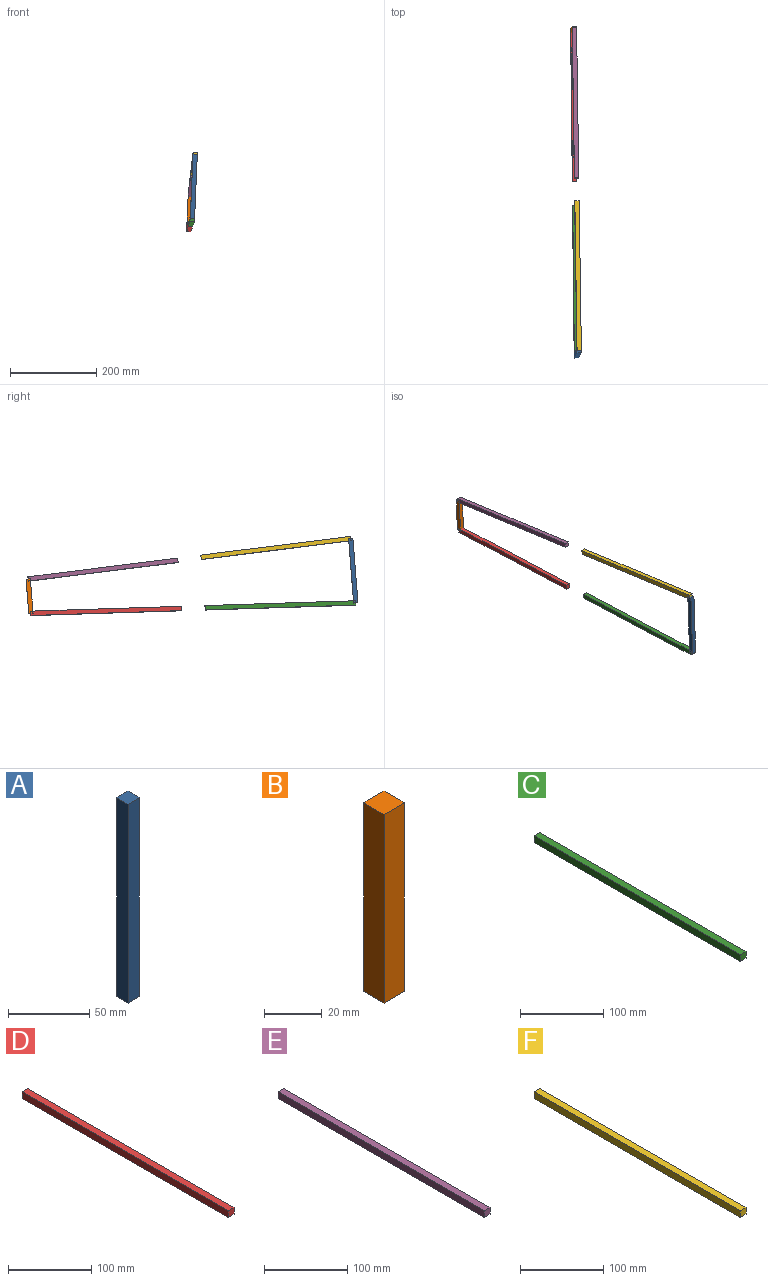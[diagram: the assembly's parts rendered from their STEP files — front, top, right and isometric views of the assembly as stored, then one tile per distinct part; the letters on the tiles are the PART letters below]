
ASSEMBLY  parts=6 mates=8
PART A: 6 faces, bbox 10x10x150 mm
  f0: plane 10x10mm, normal (0,0,1), area 100mm2, adj f1,f3,f4,f5
  f1: plane 150x10mm, normal (0,-1,0), area 1500mm2, adj f0,f2,f4,f5
  f2: plane 10x10mm, normal (0,0,-1), area 100mm2, adj f1,f3,f4,f5
  f3: plane 150x10mm, normal (0,1,0), area 1500mm2, adj f0,f2,f4,f5
  f4: plane 150x10mm, normal (1,0,0), area 1500mm2, adj f0,f1,f2,f3
  f5: plane 150x10mm, normal (-1,0,0), area 1500mm2, adj f0,f1,f2,f3
PART B: 6 faces, bbox 10x10x80 mm
  f0: plane 10x10mm, normal (0,0,1), area 100mm2, adj f1,f3,f4,f5
  f1: plane 80x10mm, normal (0,-1,0), area 800mm2, adj f0,f2,f4,f5
  f2: plane 10x10mm, normal (0,0,-1), area 100mm2, adj f1,f3,f4,f5
  f3: plane 80x10mm, normal (0,1,0), area 800mm2, adj f0,f2,f4,f5
  f4: plane 80x10mm, normal (1,0,0), area 800mm2, adj f0,f1,f2,f3
  f5: plane 80x10mm, normal (-1,0,0), area 800mm2, adj f0,f1,f2,f3
PART C: 6 faces, bbox 10x350x10 mm
  f0: plane 350x10mm, normal (0,0,1), area 3500mm2, adj f1,f3,f4,f5
  f1: plane 10x10mm, normal (0,-1,0), area 100mm2, adj f0,f2,f4,f5
  f2: plane 350x10mm, normal (0,0,-1), area 3500mm2, adj f1,f3,f4,f5
  f3: plane 10x10mm, normal (0,1,0), area 100mm2, adj f0,f2,f4,f5
  f4: plane 350x10mm, normal (1,0,0), area 3500mm2, adj f0,f1,f2,f3
  f5: plane 350x10mm, normal (-1,0,0), area 3500mm2, adj f0,f1,f2,f3
PART D: 6 faces, bbox 10x350x10 mm
  f0: plane 10x10mm, normal (0,1,0), area 100mm2, adj f1,f3,f4,f5
  f1: plane 350x10mm, normal (0,0,1), area 3500mm2, adj f0,f2,f4,f5
  f2: plane 10x10mm, normal (0,-1,0), area 100mm2, adj f1,f3,f4,f5
  f3: plane 350x10mm, normal (0,0,-1), area 3500mm2, adj f0,f2,f4,f5
  f4: plane 350x10mm, normal (1,0,0), area 3500mm2, adj f0,f1,f2,f3
  f5: plane 350x10mm, normal (-1,0,0), area 3500mm2, adj f0,f1,f2,f3
PART E: 6 faces, bbox 10x350x10 mm
  f0: plane 350x10mm, normal (0,0,-1), area 3500mm2, adj f1,f3,f4,f5
  f1: plane 10x10mm, normal (0,1,0), area 100mm2, adj f0,f2,f4,f5
  f2: plane 350x10mm, normal (0,0,1), area 3500mm2, adj f1,f3,f4,f5
  f3: plane 10x10mm, normal (0,-1,0), area 100mm2, adj f0,f2,f4,f5
  f4: plane 350x10mm, normal (1,0,0), area 3500mm2, adj f0,f1,f2,f3
  f5: plane 350x10mm, normal (-1,0,0), area 3500mm2, adj f0,f1,f2,f3
PART F: 6 faces, bbox 10x350x10 mm
  f0: plane 10x10mm, normal (0,-1,0), area 100mm2, adj f1,f3,f4,f5
  f1: plane 350x10mm, normal (0,0,-1), area 3500mm2, adj f0,f2,f4,f5
  f2: plane 10x10mm, normal (0,1,0), area 100mm2, adj f1,f3,f4,f5
  f3: plane 350x10mm, normal (0,0,1), area 3500mm2, adj f0,f2,f4,f5
  f4: plane 350x10mm, normal (1,0,0), area 3500mm2, adj f0,f1,f2,f3
  f5: plane 350x10mm, normal (-1,0,0), area 3500mm2, adj f0,f1,f2,f3
PLACE A rot(axis=(-0.87,0.47,0.12),5.2deg) t=(178.79,240.42,478.5)mm
PLACE B rot(axis=(-0.87,0.47,0.12),5.2deg) t=(179.03,428.03,525.6)mm
PLACE C rot(axis=(-0.59,0.78,0.19),3.1deg) t=(179.63,213.75,492.02)mm
PLACE D rot(axis=(-0.59,0.78,0.19),3.1deg) t=(178.44,428.63,511.83)mm
PLACE E rot(axis=(-0.94,0.32,0.09),7.6deg) t=(179.27,453.97,536.74)mm
PLACE F rot(axis=(-0.94,0.32,0.09),7.6deg) t=(178.43,229.44,467.53)mm
MATE cylindrical C.f3 <-> D.f2  axis (-0.01,1,-0.03) through (170.94,410.79,216.25)mm
MATE revolute A.f4 <-> F.f4  axis (1,0.01,-0.04) through (186.02,72.85,376.64)mm
MATE cylindrical F.f2 <-> E.f3  axis (-0.01,0.99,-0.12) through (175.87,420.05,333.3)mm
MATE revolute D.f4 <-> B.f4  axis (1,0.01,-0.04) through (171.55,814.85,203.1)mm
MATE revolute B.f4 <-> E.f4  axis (1,0.01,-0.04) through (174.9,821.15,282.78)mm
MATE slider A.f3 <-> B.f3  axis (-0.01,1,-0.08) through (177.82,71.88,301.76)mm
MATE cylindrical A.f4 <-> C.f4  axis (1,0.01,-0.04) through (179.73,61.04,227.24)mm
MATE revolute A.f4 <-> C.f4  axis (1,0.01,-0.04) through (179.73,61.04,227.24)mm
